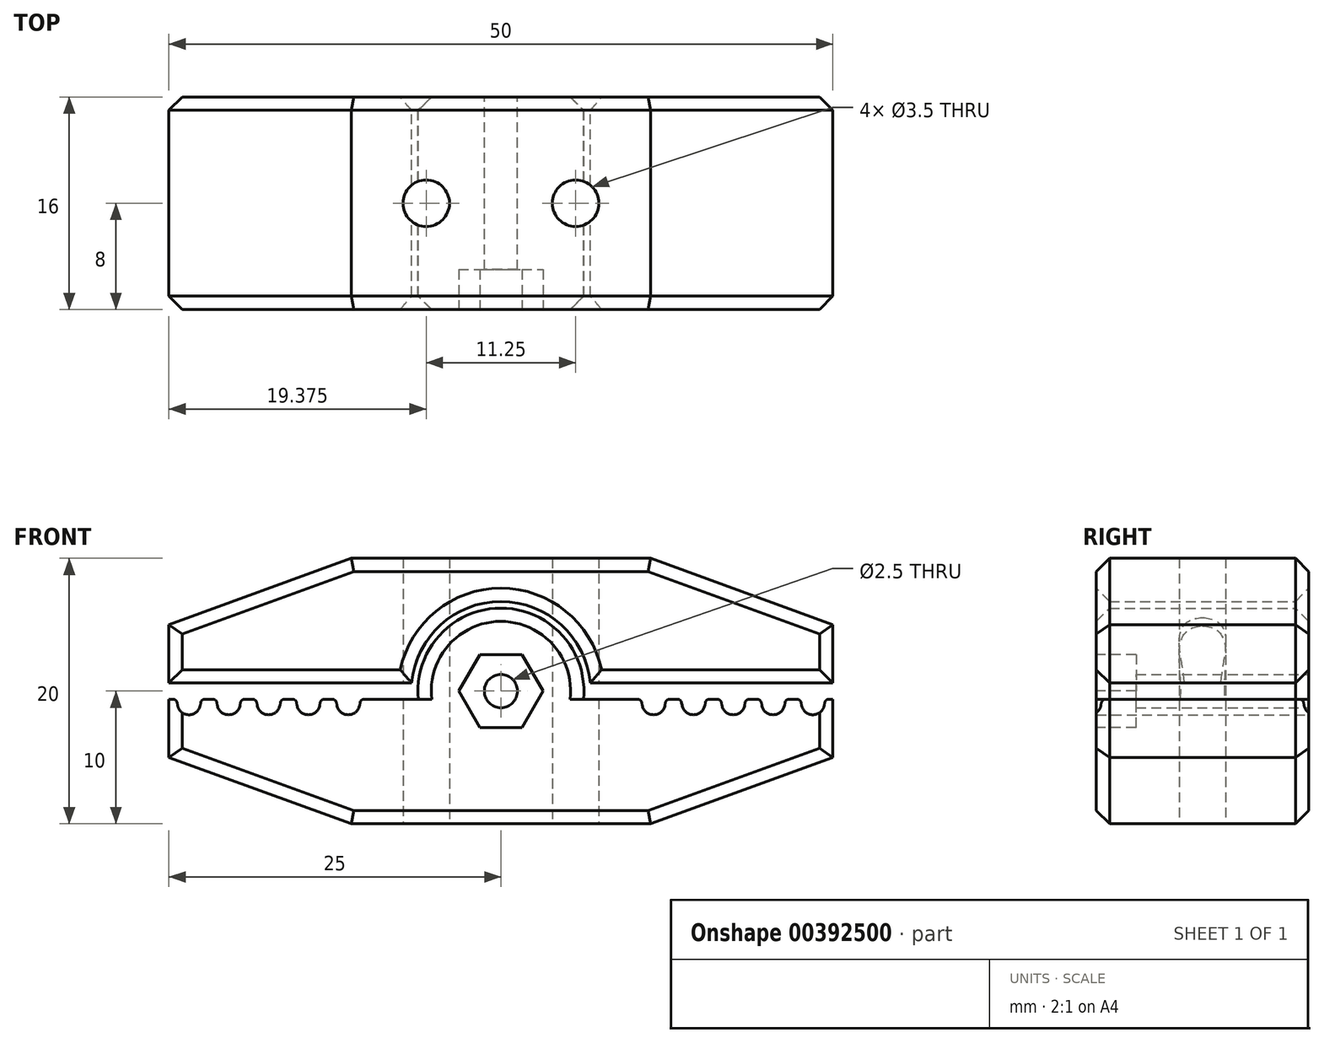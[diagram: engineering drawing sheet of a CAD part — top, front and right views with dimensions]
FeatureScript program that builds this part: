
annotation { "Feature Type Name" : "Feature", "Feature Type Description" : "" }
export const myFeature = defineFeature(function(context is Context, id is Id, definition is map)
    precondition{}
    {
        {
            var Q0;
            Q0=qCreatedBy(makeId("Front.planeOp"),FACE);
            var sketch = newSketch(context, id + "F0", { "sketchPlane" : qUnion([Q0])});
            skCircle(sketch, "E0", {"center": v(0, 0) * mm, "radius": 1.25 * mm});
            skLineSegment(sketch, "E1", {"start": v(0, 0) * mm, "end": v(11.5, 0) * mm, "construction": true});
            skLineSegment(sketch, "E2.bottom", {"start": v(10, 0.62) * mm, "end": v(13, 0.62) * mm});
            skLineSegment(sketch, "E2.left", {"start": v(10, 0.62) * mm, "end": v(10, -0.61) * mm});
            skLineSegment(sketch, "E2.right", {"start": v(13, 0.62) * mm, "end": v(13, -0.61) * mm});
            skPoint(sketch, "E2.middle", {"position": v(11.5, 0) * mm});
            skArc(sketch, "E3", {"start": v(10.64, -1.06) * mm, "mid": v(11.5, -1.78) * mm, "end": v(12.36, -1.06) * mm});
            skPoint(sketch, "E4", {"position": v(11.5, -1.78) * mm});
            skLineSegment(sketch, "E5", {"start": v(10.64, -1.06) * mm, "end": v(10.6, -0.87) * mm});
            skLineSegment(sketch, "E6", {"start": v(11.5, -0.91) * mm, "end": v(11.5, 0.62) * mm, "construction": true});
            skLineSegment(sketch, "E7.MirrorCS", {"start": v(12.36, -1.06) * mm, "end": v(12.39, -0.87) * mm});
            skLineSegment(sketch, "E8", {"start": v(10.31, -0.61) * mm, "end": v(10, -0.61) * mm});
            skLineSegment(sketch, "E9.MirrorCS", {"start": v(12.69, -0.61) * mm, "end": v(13, -0.61) * mm});
            skPoint(sketch, "E10.visualSharp", {"position": v(10.57, -0.61) * mm});
            skArc(sketch, "E10.filletArc", {"start": v(10.6, -0.87) * mm, "mid": v(10.5, -0.69) * mm, "end": v(10.31, -0.61) * mm});
            skPoint(sketch, "E11.visualSharp", {"position": v(12.43, -0.61) * mm});
            skArc(sketch, "E11.filletArc", {"start": v(12.69, -0.61) * mm, "mid": v(12.5, -0.69) * mm, "end": v(12.39, -0.87) * mm});
            skLineSegment(sketch, "E12", {"start": v(10, 0.62) * mm, "end": v(1.25, 0.62) * mm, "construction": true});
            skPoint(sketch, "E13", {"position": v(1.25, 0) * mm});
            skLineSegment(sketch, "E14", {"start": v(5.62, 0.62) * mm, "end": v(5.62, 10) * mm, "construction": true});
            skLineSegment(sketch, "E15.bottom", {"start": v(25, 10) * mm, "end": v(-25, 10) * mm});
            skLineSegment(sketch, "E15.top", {"start": v(25, -10) * mm, "end": v(-25, -10) * mm});
            skLineSegment(sketch, "E15.left", {"start": v(25, 10) * mm, "end": v(25, -10) * mm});
            skLineSegment(sketch, "E15.right", {"start": v(-25, 10) * mm, "end": v(-25, -10) * mm});
            skPoint(sketch, "E16.1.0.0", {"position": v(15.43, -0.61) * mm});
            skLineSegment(sketch, "E16.1.0.1", {"start": v(16, 0.62) * mm, "end": v(16, -0.61) * mm});
            skPoint(sketch, "E16.1.0.2", {"position": v(13.57, -0.61) * mm});
            skLineSegment(sketch, "E16.1.0.4", {"start": v(13, 0.62) * mm, "end": v(16, 0.62) * mm});
            skLineSegment(sketch, "E16.1.0.5", {"start": v(14.5, -0.91) * mm, "end": v(14.5, 0.62) * mm, "construction": true});
            skArc(sketch, "E16.1.0.6", {"start": v(13.64, -1.06) * mm, "mid": v(14.5, -1.78) * mm, "end": v(15.36, -1.06) * mm});
            skPoint(sketch, "E16.1.0.7", {"position": v(14.5, -1.78) * mm});
            skPoint(sketch, "E16.1.0.8", {"position": v(14.5, 0) * mm});
            skPoint(sketch, "E16.1.0.9", {"position": v(15.43, -0.61) * mm});
            skArc(sketch, "E16.1.0.10", {"start": v(13.6, -0.87) * mm, "mid": v(13.5, -0.69) * mm, "end": v(13.31, -0.61) * mm});
            skPoint(sketch, "E16.1.0.11", {"position": v(15.43, -0.61) * mm});
            skLineSegment(sketch, "E16.1.0.12", {"start": v(13.31, -0.61) * mm, "end": v(13, -0.61) * mm});
            skLineSegment(sketch, "E16.1.0.13", {"start": v(13.64, -1.06) * mm, "end": v(13.6, -0.87) * mm});
            skLineSegment(sketch, "E16.1.0.14", {"start": v(15.69, -0.61) * mm, "end": v(16, -0.61) * mm});
            skLineSegment(sketch, "E16.1.0.15", {"start": v(15.69, -0.61) * mm, "end": v(16, -0.61) * mm});
            skLineSegment(sketch, "E16.1.0.16", {"start": v(15.36, -1.06) * mm, "end": v(15.39, -0.87) * mm});
            skArc(sketch, "E16.1.0.17", {"start": v(15.69, -0.61) * mm, "mid": v(15.5, -0.69) * mm, "end": v(15.39, -0.87) * mm});
            skLineSegment(sketch, "E16.1.0.18", {"start": v(15.36, -1.06) * mm, "end": v(15.39, -0.87) * mm});
            skPoint(sketch, "E16.2.0.0", {"position": v(18.43, -0.61) * mm});
            skLineSegment(sketch, "E16.2.0.1", {"start": v(19, 0.62) * mm, "end": v(19, -0.61) * mm});
            skPoint(sketch, "E16.2.0.2", {"position": v(16.57, -0.61) * mm});
            skLineSegment(sketch, "E16.2.0.3", {"start": v(16, 0.62) * mm, "end": v(16, -0.61) * mm});
            skLineSegment(sketch, "E16.2.0.4", {"start": v(16, 0.62) * mm, "end": v(19, 0.62) * mm});
            skLineSegment(sketch, "E16.2.0.5", {"start": v(17.5, -0.91) * mm, "end": v(17.5, 0.62) * mm, "construction": true});
            skArc(sketch, "E16.2.0.6", {"start": v(16.64, -1.06) * mm, "mid": v(17.5, -1.78) * mm, "end": v(18.36, -1.06) * mm});
            skPoint(sketch, "E16.2.0.7", {"position": v(17.5, -1.78) * mm});
            skPoint(sketch, "E16.2.0.8", {"position": v(17.5, 0) * mm});
            skPoint(sketch, "E16.2.0.9", {"position": v(18.43, -0.61) * mm});
            skArc(sketch, "E16.2.0.10", {"start": v(16.6, -0.87) * mm, "mid": v(16.5, -0.69) * mm, "end": v(16.31, -0.61) * mm});
            skPoint(sketch, "E16.2.0.11", {"position": v(18.43, -0.61) * mm});
            skLineSegment(sketch, "E16.2.0.12", {"start": v(16.31, -0.61) * mm, "end": v(16, -0.61) * mm});
            skLineSegment(sketch, "E16.2.0.13", {"start": v(16.64, -1.06) * mm, "end": v(16.6, -0.87) * mm});
            skLineSegment(sketch, "E16.2.0.14", {"start": v(18.69, -0.61) * mm, "end": v(19, -0.61) * mm});
            skLineSegment(sketch, "E16.2.0.15", {"start": v(18.69, -0.61) * mm, "end": v(19, -0.61) * mm});
            skLineSegment(sketch, "E16.2.0.16", {"start": v(18.36, -1.06) * mm, "end": v(18.39, -0.87) * mm});
            skArc(sketch, "E16.2.0.17", {"start": v(18.69, -0.61) * mm, "mid": v(18.5, -0.69) * mm, "end": v(18.39, -0.87) * mm});
            skLineSegment(sketch, "E16.2.0.18", {"start": v(18.36, -1.06) * mm, "end": v(18.39, -0.87) * mm});
            skPoint(sketch, "E16.3.0.0", {"position": v(21.43, -0.61) * mm});
            skLineSegment(sketch, "E16.3.0.1", {"start": v(22, 0.62) * mm, "end": v(22, -0.61) * mm});
            skPoint(sketch, "E16.3.0.2", {"position": v(19.57, -0.61) * mm});
            skLineSegment(sketch, "E16.3.0.3", {"start": v(19, 0.62) * mm, "end": v(19, -0.61) * mm});
            skLineSegment(sketch, "E16.3.0.4", {"start": v(19, 0.62) * mm, "end": v(22, 0.62) * mm});
            skLineSegment(sketch, "E16.3.0.5", {"start": v(20.5, -0.91) * mm, "end": v(20.5, 0.62) * mm, "construction": true});
            skArc(sketch, "E16.3.0.6", {"start": v(19.64, -1.06) * mm, "mid": v(20.5, -1.78) * mm, "end": v(21.36, -1.06) * mm});
            skPoint(sketch, "E16.3.0.7", {"position": v(20.5, -1.78) * mm});
            skPoint(sketch, "E16.3.0.8", {"position": v(20.5, 0) * mm});
            skPoint(sketch, "E16.3.0.9", {"position": v(21.43, -0.61) * mm});
            skArc(sketch, "E16.3.0.10", {"start": v(19.6, -0.87) * mm, "mid": v(19.5, -0.69) * mm, "end": v(19.31, -0.61) * mm});
            skPoint(sketch, "E16.3.0.11", {"position": v(21.43, -0.61) * mm});
            skLineSegment(sketch, "E16.3.0.12", {"start": v(19.31, -0.61) * mm, "end": v(19, -0.61) * mm});
            skLineSegment(sketch, "E16.3.0.13", {"start": v(19.64, -1.06) * mm, "end": v(19.6, -0.87) * mm});
            skLineSegment(sketch, "E16.3.0.14", {"start": v(21.69, -0.61) * mm, "end": v(22, -0.61) * mm});
            skLineSegment(sketch, "E16.3.0.15", {"start": v(21.69, -0.61) * mm, "end": v(22, -0.61) * mm});
            skLineSegment(sketch, "E16.3.0.16", {"start": v(21.36, -1.06) * mm, "end": v(21.39, -0.87) * mm});
            skArc(sketch, "E16.3.0.17", {"start": v(21.69, -0.61) * mm, "mid": v(21.5, -0.69) * mm, "end": v(21.39, -0.87) * mm});
            skLineSegment(sketch, "E16.3.0.18", {"start": v(21.36, -1.06) * mm, "end": v(21.39, -0.87) * mm});
            skPoint(sketch, "E16.4.0.0", {"position": v(24.43, -0.61) * mm});
            skLineSegment(sketch, "E16.4.0.1", {"start": v(25, 0.62) * mm, "end": v(25, -0.61) * mm});
            skPoint(sketch, "E16.4.0.2", {"position": v(22.57, -0.61) * mm});
            skLineSegment(sketch, "E16.4.0.3", {"start": v(22, 0.62) * mm, "end": v(22, -0.61) * mm});
            skLineSegment(sketch, "E16.4.0.4", {"start": v(22, 0.62) * mm, "end": v(25, 0.62) * mm});
            skLineSegment(sketch, "E16.4.0.5", {"start": v(23.5, -0.91) * mm, "end": v(23.5, 0.62) * mm, "construction": true});
            skArc(sketch, "E16.4.0.6", {"start": v(22.64, -1.06) * mm, "mid": v(23.5, -1.78) * mm, "end": v(24.36, -1.06) * mm});
            skPoint(sketch, "E16.4.0.7", {"position": v(23.5, -1.78) * mm});
            skPoint(sketch, "E16.4.0.8", {"position": v(23.5, 0) * mm});
            skPoint(sketch, "E16.4.0.9", {"position": v(24.43, -0.61) * mm});
            skArc(sketch, "E16.4.0.10", {"start": v(22.6, -0.87) * mm, "mid": v(22.5, -0.69) * mm, "end": v(22.31, -0.61) * mm});
            skPoint(sketch, "E16.4.0.11", {"position": v(24.43, -0.61) * mm});
            skLineSegment(sketch, "E16.4.0.12", {"start": v(22.31, -0.61) * mm, "end": v(22, -0.61) * mm});
            skLineSegment(sketch, "E16.4.0.13", {"start": v(22.64, -1.06) * mm, "end": v(22.6, -0.87) * mm});
            skLineSegment(sketch, "E16.4.0.14", {"start": v(24.69, -0.61) * mm, "end": v(25, -0.61) * mm});
            skLineSegment(sketch, "E16.4.0.15", {"start": v(24.69, -0.61) * mm, "end": v(25, -0.61) * mm});
            skLineSegment(sketch, "E16.4.0.16", {"start": v(24.36, -1.06) * mm, "end": v(24.39, -0.87) * mm});
            skArc(sketch, "E16.4.0.17", {"start": v(24.69, -0.61) * mm, "mid": v(24.5, -0.69) * mm, "end": v(24.39, -0.87) * mm});
            skLineSegment(sketch, "E16.4.0.18", {"start": v(24.36, -1.06) * mm, "end": v(24.39, -0.87) * mm});
            skLineSegment(sketch, "E16.direction1", {"start": v(10, -0.61) * mm, "end": v(13, -0.61) * mm, "construction": true});
            skArc(sketch, "E17", {"start": v(6.22, -0.61) * mm, "mid": v(-4.2, 4.63) * mm, "end": v(0, -6.25) * mm});
            skPoint(sketch, "E18", {"position": v(6.25, 0) * mm});
            skLineSegment(sketch, "E19", {"start": v(10, -0.61) * mm, "end": v(6.22, -0.61) * mm});
            skLineSegment(sketch, "E20", {"start": v(10, 0.62) * mm, "end": v(6.22, 0.62) * mm});
            skPoint(sketch, "E21", {"position": v(0, 6.25) * mm});
            skPoint(sketch, "E21.positionSnap0", {"position": v(0, 10) * mm});
            skLineSegment(sketch, "E22", {"start": v(0, 0) * mm, "end": v(0, 10) * mm, "construction": true});
            skArc(sketch, "E23", {"start": v(6.72, -0.61) * mm, "mid": v(-4.55, 4.99) * mm, "end": v(0, -6.75) * mm});
            skLineSegment(sketch, "E24", {"start": v(0, 10) * mm, "end": v(0, -10) * mm});
            skLineSegment(sketch, "E25", {"start": v(25, -5) * mm, "end": v(11.26, -10) * mm});
            skLineSegment(sketch, "E26.MirrorCS", {"start": v(25, 5) * mm, "end": v(11.26, 10) * mm});
            skSolve(sketch);
        }
        {
            var Q0;
            Q0=makeQuery(id+"F0.imprint","IMPRINT",FACE,{"disambiguationData":[TD([[makeQuery(id+"F0.imprint","IMPRINT",EDGE,{"derivedFrom":sQuery(id+"F0.wireOp",EDGE,"E3")}),-1.0]])]});
            extrude(context, id + "F1", {"entities" : qUnion([Q0]), "depth" : 16 * mm, "offsetDistance" : 25 * mm});
        }
        {
            var Q0;
            {var subQ6=sQuery(id+"F0.wireOp",EDGE,"E2.bottom");Q0=makeQuery(id+"F0.imprint","IMPRINT",FACE,{"disambiguationData":[TD([[makeQuery(id+"F0.imprint","IMPRINT",EDGE,{"derivedFrom":subQ6}),1.0]])]});}
            extrude(context, id + "F2", {"entities" : qUnion([Q0]), "depth" : 16 * mm, "offsetDistance" : 25 * mm});
        }
        {
            var Q0;
            Q0=makeQuery(id+"F1.opExtrude","SWEPT_FACE",FACE,{"disambiguationData":[OSD([sQuery(id+"F0.wireOp",EDGE,"E15.top")])]});
            var sketch = newSketch(context, id + "F3", { "sketchPlane" : qUnion([Q0])});
            skLineSegment(sketch, "E27", {"start": v(5.62, 0) * mm, "end": v(5.62, 16) * mm, "construction": true});
            skCircle(sketch, "E28", {"center": v(5.62, 8) * mm, "radius": 1.75 * mm});
            skSolve(sketch);
        }
        {
            var Q0;
            Q0 = qSketchRegion(id + "F3", true);
            extrude(context, id + "F4", {"entities" : qUnion([Q0]), "operationType" : NewBodyOperationType.REMOVE, "endBound" : BoundingType.THROUGH_ALL, "oppositeDirection" : true, "depth" : 25 * mm, "offsetDistance" : 25 * mm});
        }
        {
            var Q0;
            Q0=makeQuery(id+"F1.opExtrude","SWEPT_BODY",BODY,{"disambiguationData":[OSD([sQuery(id+"F0.wireOp",EDGE,"E0"),sQuery(id+"F0.wireOp",EDGE,"E3"),sQuery(id+"F0.wireOp",EDGE,"E5"),sQuery(id+"F0.wireOp",EDGE,"E7.MirrorCS"),sQuery(id+"F0.wireOp",EDGE,"E8"),sQuery(id+"F0.wireOp",EDGE,"E9.MirrorCS"),sQuery(id+"F0.wireOp",EDGE,"E10.filletArc"),sQuery(id+"F0.wireOp",EDGE,"E11.filletArc"),sQuery(id+"F0.wireOp",EDGE,"E15.top"),sQuery(id+"F0.wireOp",EDGE,"E15.left"),sQuery(id+"F0.wireOp",EDGE,"E16.1.0.6"),sQuery(id+"F0.wireOp",EDGE,"E16.1.0.10"),sQuery(id+"F0.wireOp",EDGE,"E16.1.0.12"),sQuery(id+"F0.wireOp",EDGE,"E16.1.0.13"),sQuery(id+"F0.wireOp",EDGE,"E16.1.0.15"),sQuery(id+"F0.wireOp",EDGE,"E16.1.0.17"),sQuery(id+"F0.wireOp",EDGE,"E16.1.0.18"),sQuery(id+"F0.wireOp",EDGE,"E16.2.0.6"),sQuery(id+"F0.wireOp",EDGE,"E16.2.0.10"),sQuery(id+"F0.wireOp",EDGE,"E16.2.0.12"),sQuery(id+"F0.wireOp",EDGE,"E16.2.0.13"),sQuery(id+"F0.wireOp",EDGE,"E16.2.0.15"),sQuery(id+"F0.wireOp",EDGE,"E16.2.0.17"),sQuery(id+"F0.wireOp",EDGE,"E16.2.0.18"),sQuery(id+"F0.wireOp",EDGE,"E16.3.0.6"),sQuery(id+"F0.wireOp",EDGE,"E16.3.0.10"),sQuery(id+"F0.wireOp",EDGE,"E16.3.0.12"),sQuery(id+"F0.wireOp",EDGE,"E16.3.0.13"),sQuery(id+"F0.wireOp",EDGE,"E16.3.0.15"),sQuery(id+"F0.wireOp",EDGE,"E16.3.0.17"),sQuery(id+"F0.wireOp",EDGE,"E16.3.0.18"),sQuery(id+"F0.wireOp",EDGE,"E16.4.0.6"),sQuery(id+"F0.wireOp",EDGE,"E16.4.0.10"),sQuery(id+"F0.wireOp",EDGE,"E16.4.0.12"),sQuery(id+"F0.wireOp",EDGE,"E16.4.0.13"),sQuery(id+"F0.wireOp",EDGE,"E16.4.0.15"),sQuery(id+"F0.wireOp",EDGE,"E16.4.0.17"),sQuery(id+"F0.wireOp",EDGE,"E16.4.0.18"),sQuery(id+"F0.wireOp",EDGE,"E17"),sQuery(id+"F0.wireOp",EDGE,"E19"),sQuery(id+"F0.wireOp",EDGE,"E24"),sQuery(id+"F0.wireOp",EDGE,"E25")])]});
            var Q1;
            Q1=makeQuery(id+"F2.opExtrude","SWEPT_BODY",BODY,{"disambiguationData":[OSD([sQuery(id+"F0.wireOp",EDGE,"E2.bottom"),sQuery(id+"F0.wireOp",EDGE,"E15.bottom"),sQuery(id+"F0.wireOp",EDGE,"E15.left"),sQuery(id+"F0.wireOp",EDGE,"E16.1.0.4"),sQuery(id+"F0.wireOp",EDGE,"E16.2.0.4"),sQuery(id+"F0.wireOp",EDGE,"E16.3.0.4"),sQuery(id+"F0.wireOp",EDGE,"E16.4.0.4"),sQuery(id+"F0.wireOp",EDGE,"E20"),sQuery(id+"F0.wireOp",EDGE,"E23"),sQuery(id+"F0.wireOp",EDGE,"E24"),sQuery(id+"F0.wireOp",EDGE,"E26.MirrorCS")])]});
            var Q2;
            Q2=qCreatedBy(makeId("Right.planeOp"),FACE);
            mirror(context, id + "F5", {"operationType" : NewBodyOperationType.ADD, "entities" : qUnion([Q0, Q1]), "mirrorPlane" : qUnion([Q2])});
        }
        {
            var Q0;
            {var subQ0=makeQuery(id+"F2.opExtrude","CAP_FACE",FACE,{"disambiguationData":[OSD([sQuery(id+"F0.wireOp",EDGE,"E2.bottom"),sQuery(id+"F0.wireOp",EDGE,"E15.bottom"),sQuery(id+"F0.wireOp",EDGE,"E15.left"),sQuery(id+"F0.wireOp",EDGE,"E16.1.0.4"),sQuery(id+"F0.wireOp",EDGE,"E16.2.0.4"),sQuery(id+"F0.wireOp",EDGE,"E16.3.0.4"),sQuery(id+"F0.wireOp",EDGE,"E16.4.0.4"),sQuery(id+"F0.wireOp",EDGE,"E20"),sQuery(id+"F0.wireOp",EDGE,"E23"),sQuery(id+"F0.wireOp",EDGE,"E24"),sQuery(id+"F0.wireOp",EDGE,"E26.MirrorCS")])],"isStart":false});Q0=makeQuery(id+"F5.boolean.opBoolean","MERGE",FACE,{"derivedFrom":[subQ0,makeQuery(id+"F5.opPattern","COPY",FACE,{"derivedFrom":subQ0,"instanceName":"1"})]});}
            var Q1;
            {var subQ0=makeQuery(id+"F2.opExtrude","CAP_FACE",FACE,{"disambiguationData":[OSD([sQuery(id+"F0.wireOp",EDGE,"E2.bottom"),sQuery(id+"F0.wireOp",EDGE,"E15.bottom"),sQuery(id+"F0.wireOp",EDGE,"E15.left"),sQuery(id+"F0.wireOp",EDGE,"E16.1.0.4"),sQuery(id+"F0.wireOp",EDGE,"E16.2.0.4"),sQuery(id+"F0.wireOp",EDGE,"E16.3.0.4"),sQuery(id+"F0.wireOp",EDGE,"E16.4.0.4"),sQuery(id+"F0.wireOp",EDGE,"E20"),sQuery(id+"F0.wireOp",EDGE,"E23"),sQuery(id+"F0.wireOp",EDGE,"E24"),sQuery(id+"F0.wireOp",EDGE,"E26.MirrorCS")])],"isStart":true});Q1=makeQuery(id+"F5.boolean.opBoolean","MERGE",FACE,{"derivedFrom":[subQ0,makeQuery(id+"F5.opPattern","COPY",FACE,{"derivedFrom":subQ0,"instanceName":"1"})]});}
            var Q2;
            Q2=makeQuery(id+"F5.opPattern","COPY",EDGE,{"derivedFrom":makeQuery(id+"F1.opExtrude","CAP_EDGE",EDGE,{"disambiguationData":[OSD([sQuery(id+"F0.wireOp",EDGE,"E25")])],"isStart":false}),"instanceName":"1"});
            var Q3;
            Q3=makeQuery(id+"F1.opExtrude","CAP_EDGE",EDGE,{"disambiguationData":[OSD([sQuery(id+"F0.wireOp",EDGE,"E25")])],"isStart":false});
            var Q4;
            {var subQ0=makeQuery(id+"F1.opExtrude","CAP_EDGE",EDGE,{"disambiguationData":[OSD([sQuery(id+"F0.wireOp",EDGE,"E15.top")])],"isStart":false});Q4=makeQuery(id+"F5.boolean.opBoolean","MERGE",EDGE,{"derivedFrom":[subQ0,makeQuery(id+"F5.opPattern","COPY",EDGE,{"derivedFrom":subQ0,"instanceName":"1"})]});}
            var Q5;
            Q5=makeQuery(id+"F5.opPattern","COPY",EDGE,{"derivedFrom":makeQuery(id+"F1.opExtrude","CAP_EDGE",EDGE,{"disambiguationData":[OSD([sQuery(id+"F0.wireOp",EDGE,"E25")])],"isStart":true}),"instanceName":"1"});
            var Q6;
            {var subQ0=makeQuery(id+"F1.opExtrude","CAP_EDGE",EDGE,{"disambiguationData":[OSD([sQuery(id+"F0.wireOp",EDGE,"E15.top")])],"isStart":true});Q6=makeQuery(id+"F5.boolean.opBoolean","MERGE",EDGE,{"derivedFrom":[subQ0,makeQuery(id+"F5.opPattern","COPY",EDGE,{"derivedFrom":subQ0,"instanceName":"1"})]});}
            var Q7;
            Q7=makeQuery(id+"F1.opExtrude","CAP_EDGE",EDGE,{"disambiguationData":[OSD([sQuery(id+"F0.wireOp",EDGE,"E25")])],"isStart":true});
            var Q8;
            Q8=makeQuery(id+"F5.opPattern","COPY",EDGE,{"derivedFrom":makeQuery(id+"F1.opExtrude","CAP_EDGE",EDGE,{"disambiguationData":[OSD([sQuery(id+"F0.wireOp",EDGE,"E15.left")])],"isStart":false}),"instanceName":"1"});
            var Q9;
            Q9=makeQuery(id+"F1.opExtrude","CAP_EDGE",EDGE,{"disambiguationData":[OSD([sQuery(id+"F0.wireOp",EDGE,"E15.left")])],"isStart":false});
            var Q10;
            Q10=makeQuery(id+"F1.opExtrude","CAP_EDGE",EDGE,{"disambiguationData":[OSD([sQuery(id+"F0.wireOp",EDGE,"E15.left")])],"isStart":true});
            var Q11;
            Q11=makeQuery(id+"F5.opPattern","COPY",EDGE,{"derivedFrom":makeQuery(id+"F1.opExtrude","CAP_EDGE",EDGE,{"disambiguationData":[OSD([sQuery(id+"F0.wireOp",EDGE,"E15.left")])],"isStart":true}),"instanceName":"1"});
            var Q12;
            {var subQ0=makeQuery(id+"F1.opExtrude","CAP_EDGE",EDGE,{"disambiguationData":[OSD([sQuery(id+"F0.wireOp",EDGE,"E17")])],"isStart":true});Q12=makeQuery(id+"F5.boolean.opBoolean","MERGE",EDGE,{"derivedFrom":[subQ0,makeQuery(id+"F5.opPattern","COPY",EDGE,{"derivedFrom":subQ0,"instanceName":"1"})]});}
            var Q13;
            {var subQ0=makeQuery(id+"F1.opExtrude","CAP_EDGE",EDGE,{"disambiguationData":[OSD([sQuery(id+"F0.wireOp",EDGE,"E17")])],"isStart":false});Q13=makeQuery(id+"F5.boolean.opBoolean","MERGE",EDGE,{"derivedFrom":[subQ0,makeQuery(id+"F5.opPattern","COPY",EDGE,{"derivedFrom":subQ0,"instanceName":"1"})]});}
            chamfer(context, id + "F6", {"entities" : qUnion([Q0, Q1, Q2, Q3, Q4, Q5, Q6, Q7, Q8, Q9, Q10, Q11, Q12, Q13]), "width" : 1 * mm, "tangentPropagation" : true});
        }
        {
            var Q0;
            {var subQ0=makeQuery(id+"F1.opExtrude","CAP_FACE",FACE,{"disambiguationData":[OSD([sQuery(id+"F0.wireOp",EDGE,"E0"),sQuery(id+"F0.wireOp",EDGE,"E3"),sQuery(id+"F0.wireOp",EDGE,"E5"),sQuery(id+"F0.wireOp",EDGE,"E7.MirrorCS"),sQuery(id+"F0.wireOp",EDGE,"E8"),sQuery(id+"F0.wireOp",EDGE,"E9.MirrorCS"),sQuery(id+"F0.wireOp",EDGE,"E10.filletArc"),sQuery(id+"F0.wireOp",EDGE,"E11.filletArc"),sQuery(id+"F0.wireOp",EDGE,"E15.top"),sQuery(id+"F0.wireOp",EDGE,"E15.left"),sQuery(id+"F0.wireOp",EDGE,"E16.1.0.6"),sQuery(id+"F0.wireOp",EDGE,"E16.1.0.10"),sQuery(id+"F0.wireOp",EDGE,"E16.1.0.12"),sQuery(id+"F0.wireOp",EDGE,"E16.1.0.13"),sQuery(id+"F0.wireOp",EDGE,"E16.1.0.15"),sQuery(id+"F0.wireOp",EDGE,"E16.1.0.17"),sQuery(id+"F0.wireOp",EDGE,"E16.1.0.18"),sQuery(id+"F0.wireOp",EDGE,"E16.2.0.6"),sQuery(id+"F0.wireOp",EDGE,"E16.2.0.10"),sQuery(id+"F0.wireOp",EDGE,"E16.2.0.12"),sQuery(id+"F0.wireOp",EDGE,"E16.2.0.13"),sQuery(id+"F0.wireOp",EDGE,"E16.2.0.15"),sQuery(id+"F0.wireOp",EDGE,"E16.2.0.17"),sQuery(id+"F0.wireOp",EDGE,"E16.2.0.18"),sQuery(id+"F0.wireOp",EDGE,"E16.3.0.6"),sQuery(id+"F0.wireOp",EDGE,"E16.3.0.10"),sQuery(id+"F0.wireOp",EDGE,"E16.3.0.12"),sQuery(id+"F0.wireOp",EDGE,"E16.3.0.13"),sQuery(id+"F0.wireOp",EDGE,"E16.3.0.15"),sQuery(id+"F0.wireOp",EDGE,"E16.3.0.17"),sQuery(id+"F0.wireOp",EDGE,"E16.3.0.18"),sQuery(id+"F0.wireOp",EDGE,"E16.4.0.6"),sQuery(id+"F0.wireOp",EDGE,"E16.4.0.10"),sQuery(id+"F0.wireOp",EDGE,"E16.4.0.12"),sQuery(id+"F0.wireOp",EDGE,"E16.4.0.13"),sQuery(id+"F0.wireOp",EDGE,"E16.4.0.15"),sQuery(id+"F0.wireOp",EDGE,"E16.4.0.17"),sQuery(id+"F0.wireOp",EDGE,"E16.4.0.18"),sQuery(id+"F0.wireOp",EDGE,"E17"),sQuery(id+"F0.wireOp",EDGE,"E19"),sQuery(id+"F0.wireOp",EDGE,"E24"),sQuery(id+"F0.wireOp",EDGE,"E25")])],"isStart":false});Q0=makeQuery(id+"F5.boolean.opBoolean","MERGE",FACE,{"derivedFrom":[subQ0,makeQuery(id+"F5.opPattern","COPY",FACE,{"derivedFrom":subQ0,"instanceName":"1"})]});}
            var sketch = newSketch(context, id + "F7", { "sketchPlane" : qUnion([Q0])});
            skCircle(sketch, "E29.cCircle", {"center": v(0, 0) * mm, "radius": 2.75 * mm, "construction": true});
            skLineSegment(sketch, "E29.0", {"start": v(1.59, 2.75) * mm, "end": v(3.18, 0) * mm});
            skLineSegment(sketch, "E29.1", {"start": v(3.18, 0) * mm, "end": v(1.59, -2.75) * mm});
            skLineSegment(sketch, "E29.2", {"start": v(1.59, -2.75) * mm, "end": v(-1.59, -2.75) * mm});
            skLineSegment(sketch, "E29.3", {"start": v(-1.59, -2.75) * mm, "end": v(-3.18, 0) * mm});
            skLineSegment(sketch, "E29.4", {"start": v(-3.18, 0) * mm, "end": v(-1.59, 2.75) * mm});
            skLineSegment(sketch, "E29.5", {"start": v(-1.59, 2.75) * mm, "end": v(1.59, 2.75) * mm});
            skPoint(sketch, "E29.0.midPoint", {"position": v(2.38, 1.38) * mm});
            skSolve(sketch);
        }
        {
            var Q0;
            Q0 = qSketchRegion(id + "F7", true);
            extrude(context, id + "F8", {"entities" : qUnion([Q0]), "operationType" : NewBodyOperationType.REMOVE, "oppositeDirection" : true, "depth" : 3 * mm, "offsetDistance" : 25 * mm});
        }
    });
